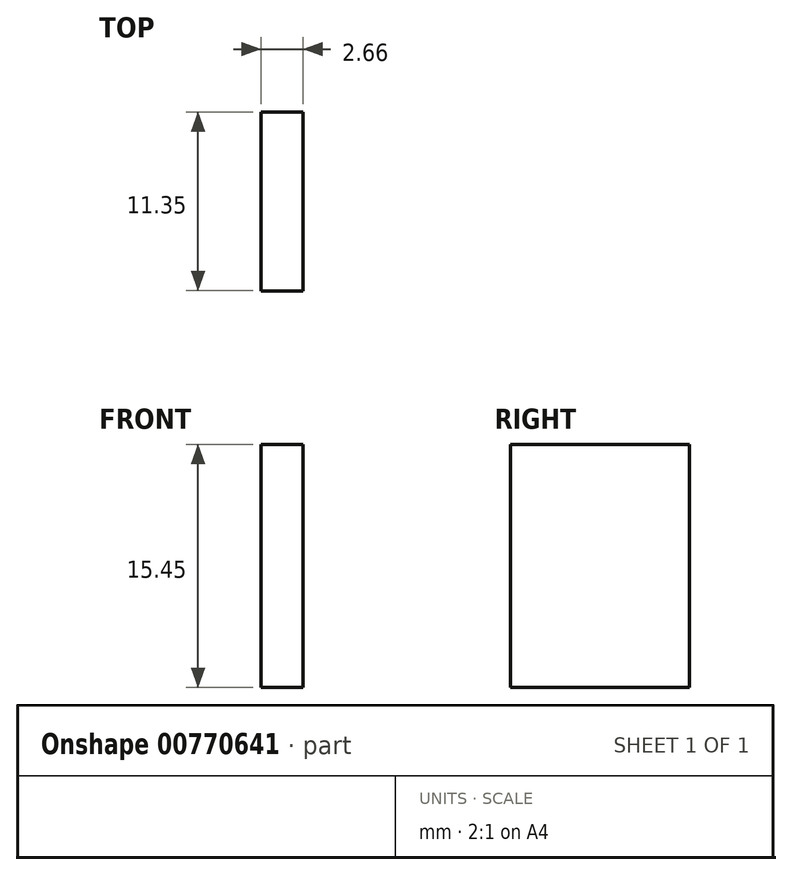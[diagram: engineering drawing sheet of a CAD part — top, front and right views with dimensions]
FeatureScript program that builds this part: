
annotation { "Feature Type Name" : "Feature", "Feature Type Description" : "" }
export const myFeature = defineFeature(function(context is Context, id is Id, definition is map)
    precondition{}
    {
        {
            var Q0;
            Q0=qCreatedBy(makeId("Front.planeOp"),FACE);
            var sketch = newSketch(context, id + "F0", { "sketchPlane" : qUnion([Q0])});
            skLineSegment(sketch, "E0", {"start": v(-74.08, 34.32) * mm, "end": v(-71.42, 34.32) * mm});
            skLineSegment(sketch, "E1", {"start": v(-71.42, 18.87) * mm, "end": v(-74.08, 18.87) * mm});
            skLineSegment(sketch, "E2", {"start": v(-74.08, 18.87) * mm, "end": v(-74.08, 34.32) * mm});
            skLineSegment(sketch, "E3", {"start": v(-71.42, 34.32) * mm, "end": v(-71.42, 18.87) * mm});
            skSolve(sketch);
        }
        {
            var Q0;
            Q0=makeQuery(id+"F0.imprint","IMPRINT",FACE,{"disambiguationData":[TD([[makeQuery(id+"F0.imprint","IMPRINT",EDGE,{"derivedFrom":sQuery(id+"F0.wireOp",EDGE,"E0")}),-1.0]])]});
            extrude(context, id + "F1", {"entities" : qUnion([Q0]), "depth" : 11.35 * mm, "offsetDistance" : 25.4 * mm});
        }
    });
